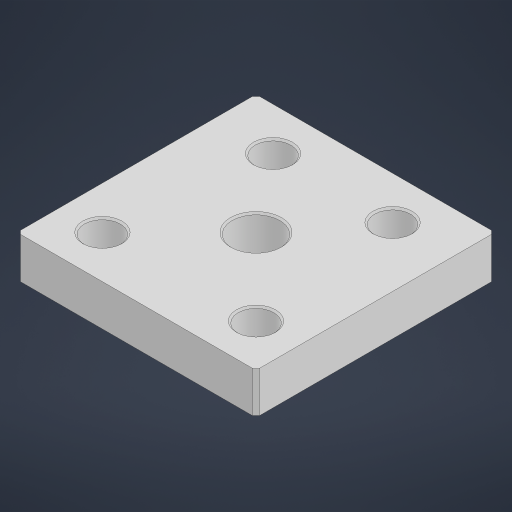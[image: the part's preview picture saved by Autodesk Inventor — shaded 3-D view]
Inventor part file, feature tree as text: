
AUTODESK INVENTOR PART (.ipt)
format: ipt  version: 2024.3 (Build 283343000, 343)  size: 202,240 bytes
history: native  units: mm
features: chamfer x2, sketch x1, extrude x1, hole x1
ambient origin geometry x8: Origin, YZ Plane, XZ Plane, XY Plane, X Axis, Y Axis, Z Axis, Center Point
bodies: Solid1 (feature_tree)
feature tree (5):
  sketch  "Sketch1"  dims[d0=70.0mm d1=45.0mm d2=35.0mm d3=14.0mm d4=12.0mm d5=0.0mm d6=10.5mm d7=20.0mm d8=4.0mm d9=2.0mm d10=90.0deg d11=8.0mm d12=20.594885mm d13=0.5mm d14=2.0mm d15=45.0deg d16=70.0mm d17=45.0mm d18=1.0mm d19=2.0mm d20=45.0deg]
  extrude  "Extrusion1"  Depth=70.0mm
  hole  "Hole1"  [1 undecoded]
  chamfer  "Chamfer1"  Distance=14.0mm
  chamfer  "Chamfer2"  Distance=12.0mm
note: 1 required parameter value undecoded (feature->parameter linkage not recoverable at this tier; creation-order binding heuristic only, values carry confidence <= 0.55)
